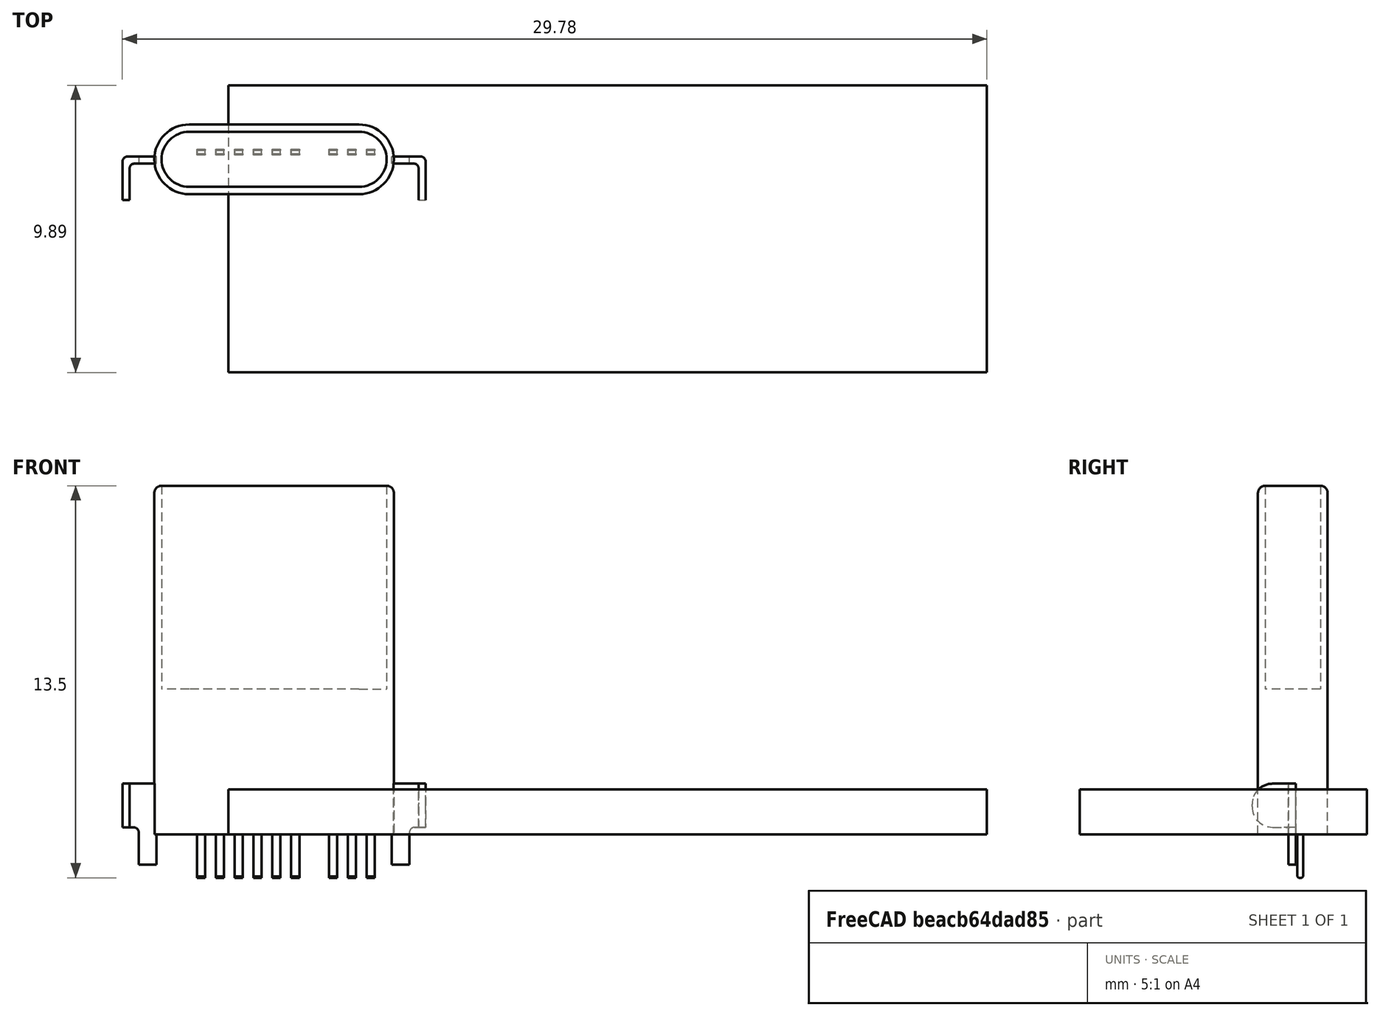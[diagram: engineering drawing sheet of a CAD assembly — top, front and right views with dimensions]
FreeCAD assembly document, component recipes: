
FREECAD ASSEMBLY — COMPONENT RECIPES ("Dual Type-C Connector")

This assembly document has 3 components, labeled P0..P2 below (a component is one placed body or linked part). 1 of them carries a construction recipe — the FreeCAD feature program that regenerates the part from scratch, quoted from this document or its linked companion documents; the rest are supplied as boundary geometry only. No exploded tour is included for this assembly.
COMPONENT P0 — recipe-attached ("Board001", modeled in this document).
Construction recipe (the document's own serialized feature program — sketch geometry with constraints, then the solid features built on it; lengths are millimeters unless a unit is written):

FEATURE [Sketcher::SketchObject] Sketch
  ArcFitTolerance = 1e-06
  AttachmentSupport = -> [XY_Plane001]
  FullyConstrained = false
  MakeInternals = false
  MapMode = 5
  sketch-geometry (4):
    g0: LineSegment StartX=-1.57833 StartY=2.5515 StartZ=0 EndX=-1.57833 EndY=-7.3385 EndZ=0
    g1: LineSegment StartX=-1.57833 StartY=-7.3385 StartZ=0 EndX=24.5517 EndY=-7.3385 EndZ=0
    g2: LineSegment StartX=24.5517 StartY=-7.3385 StartZ=0 EndX=24.5517 EndY=2.5515 EndZ=0
    g3: LineSegment StartX=24.5517 StartY=2.5515 StartZ=0 EndX=-1.57833 EndY=2.5515 EndZ=0
  constraints (10):
    c: Coincident(g0,g1)
    c: Coincident(g1,g2)
    c: Coincident(g2,g3)
    c: Coincident(g3,g0)
    c: Vertical(g0)
    c: Vertical(g2)
    c: Horizontal(g1)
    c: Horizontal(g3)
    c: DistanceY(g0,g0) = 9.89
    c: DistanceX(g3,g3) = 26.13
FEATURE [PartDesign::Pad] Pad
  Direction = (0,0,1)
  Length = 1.54
  Length2 = 10
  Profile = -> Sketch
  ReferenceAxis = -> Sketch [N_Axis]
  Refine = true
  Suppressed = false
  Type = 0
FEATURE [PartDesign::Body] Body  label="Board"
  AllowCompound = false
  Group = -> [Sketch,Pad]
  Origin = -> Origin001
  Tip = -> Pad
COMPONENT P1 — geometry summary ("Type C Male Connector001"; no construction recipe available for this part):
  bounding box: 13.5 x 10.5 x 2.6 mm
  tessellated surface: 10,420 triangles
  volume: 128 mm^3 (35% of its bounding box)
COMPONENT P2 — geometry summary ("Type C Male Connector002"; no construction recipe available for this part):
  bounding box: 13.5 x 10.5 x 2.6 mm
  tessellated surface: 10,420 triangles
  volume: 128 mm^3 (35% of its bounding box)
PROVENANCE & LICENSES
A FreeCAD (.FCStd) document from a public repository crawl; recipes are the document's own serialized feature recipes (and, for linked parts, companion documents' recipes).
License: as declared in the source repository (recorded in the dataset sidecar).
